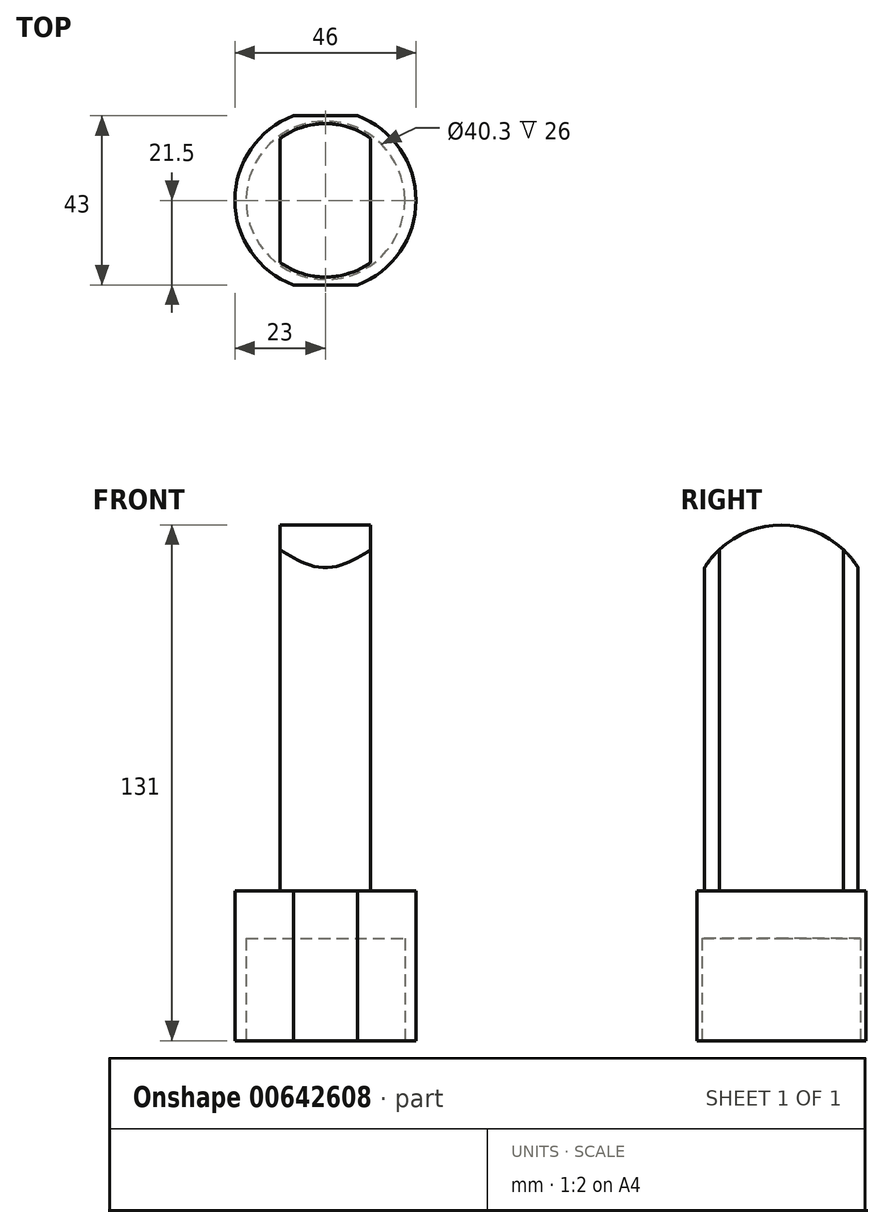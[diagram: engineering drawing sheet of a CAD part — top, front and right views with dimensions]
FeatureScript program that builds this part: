
annotation { "Feature Type Name" : "Feature", "Feature Type Description" : "" }
export const myFeature = defineFeature(function(context is Context, id is Id, definition is map)
    precondition{}
    {
        {
            var Q0;
            Q0=qCreatedBy(makeId("Top.planeOp"),FACE);
            var sketch = newSketch(context, id + "F0", { "sketchPlane" : qUnion([Q0])});
            skArc(sketch, "E0", {"start": v(-8.17, 21.5) * mm, "mid": v(-23, 0) * mm, "end": v(-8.17, -21.5) * mm});
            skLineSegment(sketch, "E1", {"start": v(-8.17, -21.5) * mm, "end": v(8.17, -21.5) * mm});
            skLineSegment(sketch, "E2.MirrorCS", {"start": v(-8.17, 21.5) * mm, "end": v(8.17, 21.5) * mm});
            skArc(sketch, "E3.trimOffspring", {"start": v(8.17, -21.5) * mm, "mid": v(23, 0) * mm, "end": v(8.17, 21.5) * mm});
            skSolve(sketch);
        }
        {
            var Q0;
            Q0 = qSketchRegion(id + "F0", true);
            var Q1;
            Q1=makeQuery(id+"F0.imprint","IMPRINT",FACE,{"disambiguationData":[TD([[makeQuery(id+"F0.imprint","IMPRINT",EDGE,{"derivedFrom":sQuery(id+"F0.wireOp",EDGE,"E0")}),1.0]])]});
            extrude(context, id + "F1", {"entities" : qUnion([Q0, Q1]), "depth" : 38 * mm, "offsetDistance" : 25 * mm});
        }
        {
            var Q0;
            Q0=makeQuery(id+"F1.opExtrude","CAP_FACE",FACE,{"disambiguationData":[OSD([sQuery(id+"F0.wireOp",EDGE,"E0"),sQuery(id+"F0.wireOp",EDGE,"E1"),sQuery(id+"F0.wireOp",EDGE,"E2.MirrorCS"),sQuery(id+"F0.wireOp",EDGE,"E3.trimOffspring")])],"isStart":true});
            var sketch = newSketch(context, id + "F2", { "sketchPlane" : qUnion([Q0])});
            skCircle(sketch, "E4", {"center": v(0, 0) * mm, "radius": 20.15 * mm});
            skSolve(sketch);
        }
        {
            var Q0;
            Q0=makeQuery(id+"F2.imprint","IMPRINT",FACE,{"disambiguationData":[TD([[makeQuery(id+"F2.imprint","IMPRINT",EDGE,{"derivedFrom":sQuery(id+"F2.wireOp",EDGE,"E4")}),1.0]])]});
            extrude(context, id + "F3", {"entities" : qUnion([Q0]), "operationType" : NewBodyOperationType.REMOVE, "oppositeDirection" : true, "depth" : 26 * mm, "offsetDistance" : 25 * mm});
        }
        {
            var Q0;
            Q0=makeQuery(id+"F1.opExtrude","CAP_FACE",FACE,{"disambiguationData":[OSD([sQuery(id+"F0.wireOp",EDGE,"E0"),sQuery(id+"F0.wireOp",EDGE,"E1"),sQuery(id+"F0.wireOp",EDGE,"E2.MirrorCS"),sQuery(id+"F0.wireOp",EDGE,"E3.trimOffspring")])],"isStart":false});
            var sketch = newSketch(context, id + "F4", { "sketchPlane" : qUnion([Q0])});
            skArc(sketch, "E5", {"start": v(-11.5, -15.75) * mm, "mid": v(0, -19.5) * mm, "end": v(11.5, -15.75) * mm});
            skLineSegment(sketch, "E6", {"start": v(-11.5, 15.75) * mm, "end": v(-11.5, -15.75) * mm});
            skLineSegment(sketch, "E7.MirrorCS", {"start": v(11.5, 15.75) * mm, "end": v(11.5, -15.75) * mm});
            skArc(sketch, "E8.trimOffspring", {"start": v(11.5, 15.75) * mm, "mid": v(0, 19.5) * mm, "end": v(-11.5, 15.75) * mm});
            skSolve(sketch);
        }
        {
            var Q0;
            Q0=makeQuery(id+"F4.imprint","IMPRINT",FACE,{"disambiguationData":[TD([[makeQuery(id+"F4.imprint","IMPRINT",EDGE,{"derivedFrom":sQuery(id+"F4.wireOp",EDGE,"E5")}),1.0]])]});
            extrude(context, id + "F5", {"entities" : qUnion([Q0]), "operationType" : NewBodyOperationType.ADD, "depth" : 93 * mm, "offsetDistance" : 25 * mm});
        }
        {
            var Q0;
            Q0=makeQuery(id+"F5.opExtrude","SWEPT_FACE",FACE,{"disambiguationData":[OSD([sQuery(id+"F4.wireOp",EDGE,"E7.MirrorCS")])]});
            var sketch = newSketch(context, id + "F6", { "sketchPlane" : qUnion([Q0])});
            skArc(sketch, "E9", {"start": v(21.05, 117.28) * mm, "mid": v(-3.1, 130.8) * mm, "end": v(-22.76, 111.33) * mm});
            skLineSegment(sketch, "E10", {"start": v(21.05, 117.28) * mm, "end": v(34.09, 153.62) * mm});
            skLineSegment(sketch, "E11", {"start": v(34.09, 153.62) * mm, "end": v(-12.18, 165.92) * mm});
            skLineSegment(sketch, "E12", {"start": v(-12.18, 165.92) * mm, "end": v(-50.2, 126.1) * mm});
            skLineSegment(sketch, "E13", {"start": v(-50.2, 126.1) * mm, "end": v(-22.76, 111.33) * mm});
            skSolve(sketch);
        }
        {
            var Q0;
            {var subQ0=sQuery(id+"F6.wireOp",EDGE,"E10");Q0=makeQuery(id+"F6.imprint","IMPRINT",FACE,{"disambiguationData":[TD([[makeQuery(id+"F6.imprint","IMPRINT",EDGE,{"derivedFrom":subQ0}),1.0]])]});}
            var Q1;
            {var subQ0=sQuery(id+"F6.wireOp",EDGE,"E9");var subQ1=sQuery(id+"F4.wireOp",EDGE,"E7.MirrorCS");var subQ4=makeQuery(id+"F5.opExtrude","CAP_EDGE",EDGE,{"disambiguationData":[OSD([subQ1])],"isStart":false});var subQ5=makeQuery(id+"F6.imprint","INTERSECT",VERTEX,{"derivedFrom":[subQ4,subQ0]});Q1=makeQuery(id+"F6.imprint","IMPRINT",FACE,{"disambiguationData":[TD([[makeQuery(id+"F6.imprint","IMPRINT",EDGE,{"disambiguationData":[TD([[subQ5,-1.0]])],"derivedFrom":subQ0}),-1.0]])]});}
            var Q2;
            {var subQ0=sQuery(id+"F6.wireOp",EDGE,"E9");var subQ1=sQuery(id+"F4.wireOp",EDGE,"E7.MirrorCS");var subQ4=makeQuery(id+"F5.opExtrude","CAP_EDGE",EDGE,{"disambiguationData":[OSD([subQ1])],"isStart":false});var subQ5=makeQuery(id+"F6.imprint","INTERSECT",VERTEX,{"derivedFrom":[subQ4,subQ0]});Q2=makeQuery(id+"F6.imprint","IMPRINT",FACE,{"disambiguationData":[TD([[makeQuery(id+"F6.imprint","IMPRINT",EDGE,{"disambiguationData":[TD([[subQ5,1.0]])],"derivedFrom":subQ0}),-1.0]])]});}
            extrude(context, id + "F7", {"entities" : qUnion([Q0, Q1, Q2]), "operationType" : NewBodyOperationType.REMOVE, "endBound" : BoundingType.THROUGH_ALL, "oppositeDirection" : true, "depth" : 25 * mm, "offsetDistance" : 25 * mm});
        }
    });
